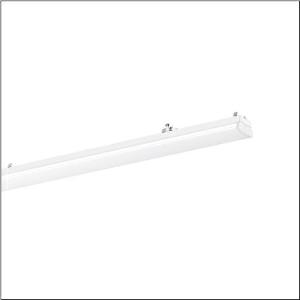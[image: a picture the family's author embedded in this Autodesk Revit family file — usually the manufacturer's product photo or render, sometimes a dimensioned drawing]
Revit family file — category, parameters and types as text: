
# Revit family: licross_r__21_recessed_opal_mo_52tl1d7n46xg_6fbc
name_source: partatom
category: Lighting Fixtures
units: mm (PartAtom-declared; Revit-internal decimal feet)

## family parameters
Cut with Voids When Loaded = No
Host = Face
Light Source = No
Part Type = Normal
Room Calculation Point = No
Round Connector Dimension = Use Diameter
Shared = No

## types (1)
- Licross® 21 recessed opal MO (1 x LED, 6200 lm, 34.9 W, 4000K)
    Apparent Load = 35 VA
    CIE Flux Codes = 44 73 91 87 100
    Color Rendering = 80
    Color Temperature = 4000K
    Default Elevation = 1800 mm
    Description = Licross® 21 recessed opal MO, luminaire insert, of sheet steel, galvanised, coil coated, white, length: 1.500mm, width: 66mm, height: 67mm, LED rated luminous flux: 6.200lm, light colour: 840, control gear: ON/OFF, with plug, 3-pole, with phase selection, mains connection: 220..240V, AC, 50/60Hz, rated input power: 35W, halogen-free wiring, primary optical cover: cover, of PMMA, light emission: direct with ceiling illumination distribution, primary light characteristic: symmetric, protection rating (complete): IP40, insulation class (complete): insulation class I (protective earthing), certification: CE, ENEC, VDE, UKCA, protection symbol: D if used in an environment without relevant dust loads with corresponding accessories, impact resistance: IK06, permissible ambient temperature for indoor applications: -35..+50°C, corresponds to IFS (International Featured Standards) requirements for safety and quality in the food industry, reducing of maximum allowable ambient temperature of 5°C with ceiling mounting, LABS conformity tested according to VDMA 24364:2018-05, packaging unit: 1 piece
    Height = 83 mm
    Lamp = 1 x LED
    Lamp Light Flux = 6200 lm
    Lamp Power = 34.9 W
    Lamp count = 1
    Length = 1500 mm
    Luminous efficacy = 178 lm/W
    Manufacturer = Siteco
    ModVariant = No
    Model = 52TL1D7N46XG
    Mounting Place = Ceiling
    Mounting Type = Pendant
    Number of Poles = 1
    OnlyDefault = Yes
    Power Factor = 1
    Product Name = Licross® 21 recessed opal MO
    Product group = luminaire insert
    ProductGroupID = 901
    Protection Class = Protection class I
    Protection Degree = IP 40
    RLX_Detail_Level = 1
    RLX_Emergency_Light_Flux = 0 lm
    RLX_Emergency_Type = 0
    RLX_Emergency_Type_DB = No
    RlxData = <blob elided: 23149 chars, md5=7fb5cea0>
    Socket = socket
    Standby Power = 0 W
    System Light Flux = 6200 lm
    System Power = 35 W
    Type Comments = Product without accessories
    Type Image = l_1313666.jpg
    URL = http://relux.com
    VarID = ---
    Voltage = 0 V
    Weight = 0.00 kg
    Width = 76 mm

## geometry (parser evidence)
native form markers: Blend x4, Sweep x13
no freeform markers — native parametric forms only
